# Revit family: PRD_FrankeWS_ShwrHds_HandShower_ACXX2007
name_source: partatom
category: Specialty Equipment
revit_build: Autodesk Revit 2018 (Build: 20190510_1515(x64)
units: mm (PartAtom-declared; Revit-internal decimal feet)

## family parameters
Always vertical = Yes
Cut with Voids When Loaded = No
OmniClass Number = 23.45.05.14.17
OmniClass Title = Showers
Part Type = Normal
Room Calculation Point = No
Round Connector Dimension = Use Diameter
Shared = No
Work Plane-Based = Yes

## types (1)
- ACXX2007
    AssetType = Fixed
    BIMObjectName = PRD_AR_ShowerHeads_HandShower_ACXX2007
    BodyMaterial = PRD_AR_ChromatedBrass_HighPolished
    Category = Pr_40_20_87_76, Shower heads
    Color = Chrome
    Default Elevation = 1219 mm
    Description = Hand shower made from chrome-plated plastic with rain jet, one jet type, diameter 110 mm, anti-scale system and low aerosol formation. Including nylon-reinforced, chrome-coloured shower hose. With twistable conical hand shower connection G 1/2 and knurled tap connection G 1/2, length 1500 mm.
    DrainSize = 15 mm  [stored 0.0492126 ft]
    DurationUnit = year
    Features = diameter 110 mm, length 1500 mm
    Finish = chromed
    GrossWeight = 0.64 kg
    HasTray = FALSE
    IfcExportAs = IfcSanitaryTerminalType
    IfcExportType = SHOWER
    Manufacturer = KWC Group AG
    ManufacturerName = KWC Group AG
    ManufacturerURL = www.kwc.com
    Model = ACXX2007
    ModelNumber = 2030051216
    ModelReference = ACXX2007
    NBSDescription = Shower heads
    NBSReference = 45-35-70/333
    Name = Hand shower ACXX2007
    NetWeight = 0.60 kg
    NominalDepth = 0 mm  [stored 0 ft]
    NominalHeight = 0 mm  [stored 0 ft]
    NominalWidth = 0 mm  [stored 0 ft]
    ProductCode = 210.0577.602
    ProductInformation = https://pim.kwc.com
    Quantity = 1
    QuantityUom = Piece
    ShowerHeadDescription = Shower head
    ShowerType = Individual
    TailorMade = No
    URL = www.kwc.com
    Uniclass2015Code = Pr_40_20_87_76
    Uniclass2015Title = Shower heads
    Uniclass2015Version = Products v1.17
    Version = 1
    WarrantyDurationUnit = year

note: [stored X ft] marks values corroborated as IEEE doubles in the binary element streams (Revit-internal decimal feet)

## geometry (parser evidence)
native form markers: Sweep x3
no freeform markers — native parametric forms only
